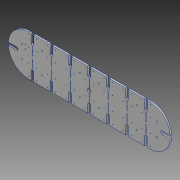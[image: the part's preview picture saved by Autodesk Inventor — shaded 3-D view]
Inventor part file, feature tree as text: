
AUTODESK INVENTOR PART (.ipt)
format: ipt  version: 2020 (Build 240168000, 168)  size: 714,752 bytes
history: native  units: mm
features: extrude x5, sketch x5
ambient origin geometry x8: Origin, YZ Plane, XZ Plane, XY Plane, X Axis, Y Axis, Z Axis, Center Point
bodies: Body1 (feature_tree)
feature tree (10):
  extrude  "Extrusion2"  Depth=86.0mm
  extrude  "Extrusion3"  Depth=432.0mm
  extrude  "Extrusion9"  Depth=10.0mm
  extrude  "Extrusion10"  Depth=10.0mm
  extrude  "Extrusion11"  Depth=10.0mm
  sketch  "Sketch1"  dims[d0=172.0mm d1=86.0mm]
  sketch  "Sketch2"  dims[d2=864.0mm d3=432.0mm]
  sketch  "Sketch9"  dims[d4=60.0mm d5=60.0mm]
  sketch  "Sketch11"  dims[d6=10.0mm d14=150.0mm d15=150.0mm d16=150.0mm d17=150.0mm d18=150.0mm d19=150.0mm d20=10.0mm]
  sketch  "Sketch12"  dims[d33=10.0mm d34=0.0mm d43=76.0mm d44=76.0mm d45=76.0mm d46=76.0mm d47=260.0mm d51=8.0mm d52=260.0mm d53=0.0mm d63=26.0mm d113=60.0mm d114=60.0mm d117=60.0mm d122=135.0mm d125=135.0mm d129=0.0mm d130=86.0mm d131=60.0mm d132=60.0mm d133=60.0mm d134=146.0mm d137=0.0mm d138=38.0mm d139=48.0mm d140=48.0mm d141=38.0mm d142=38.0mm d143=48.0mm d144=48.0mm d145=38.0mm d166=960.0mm d167=76.0mm d168=76.0mm d169=76.0mm d170=76.0mm d178=20.0mm d179=135.0mm d181=135.0mm d182=135.0mm d183=135.0mm d185=10.0mm d196=4.0mm d197=20.0mm d199=7.0mm d200=10.0mm d202=10.0mm d204=20.0mm d205=80.0mm d207=7.0mm d208=10.0mm d210=10.0mm d212=10.0mm d213=0.0mm d225=20.0mm d227=7.0mm d228=10.0mm d230=10.0mm d232=57.5mm d233=57.5mm d234=57.5mm d235=57.5mm d236=57.5mm d237=57.5mm d238=57.5mm d239=57.5mm d242=20.0mm d243=60.0mm d244=20.0mm d245=10.0mm d246=20.0mm d250=3.8mm d260=20.0mm d261=20.0mm d262=0.0mm d263=0.0mm d264=3.8mm d265=3.8mm d266=3.8mm d267=3.8mm d268=3.8mm d269=3.8mm d270=20.0mm d271=20.0mm d272=20.0mm d273=20.0mm d274=20.0mm d275=20.0mm d276=20.0mm d277=20.0mm d278=20.0mm d279=20.0mm d280=20.0mm d281=20.0mm d283=20.0mm d285=10.0mm d287=80.0mm d289=10.0mm d291=20.0mm d293=10.0mm d299=20.0mm d301=10.0mm d303=80.0mm d305=10.0mm d307=20.0mm d309=10.0mm d315=20.0mm d317=10.0mm d319=80.0mm d321=10.0mm d323=20.0mm d325=10.0mm d326=4.0mm d327=7.0mm d328=7.0mm d329=7.0mm d331=20.0mm d333=10.0mm d335=80.0mm d337=10.0mm d339=20.0mm d341=10.0mm d342=4.0mm d343=7.0mm d344=7.0mm d345=7.0mm d347=20.0mm d349=10.0mm d351=80.0mm d353=10.0mm d355=20.0mm d357=10.0mm d358=4.0mm d359=7.0mm d360=7.0mm d361=7.0mm d363=20.0mm d365=10.0mm d367=80.0mm d369=10.0mm d371=20.0mm d373=10.0mm d374=4.0mm d375=7.0mm d376=7.0mm d377=7.0mm d379=20.0mm d381=10.0mm d383=80.0mm d385=10.0mm d387=20.0mm d389=10.0mm d390=4.0mm d391=7.0mm d392=7.0mm d393=7.0mm d395=20.0mm d397=10.0mm d399=80.0mm d401=10.0mm d403=20.0mm d405=10.0mm d406=4.0mm d407=7.0mm d408=7.0mm d409=7.0mm d410=10.0mm d411=0.0mm d416=5.11mm d417=5.11mm d419=30.0mm d420=40.5mm d421=30.0mm]
